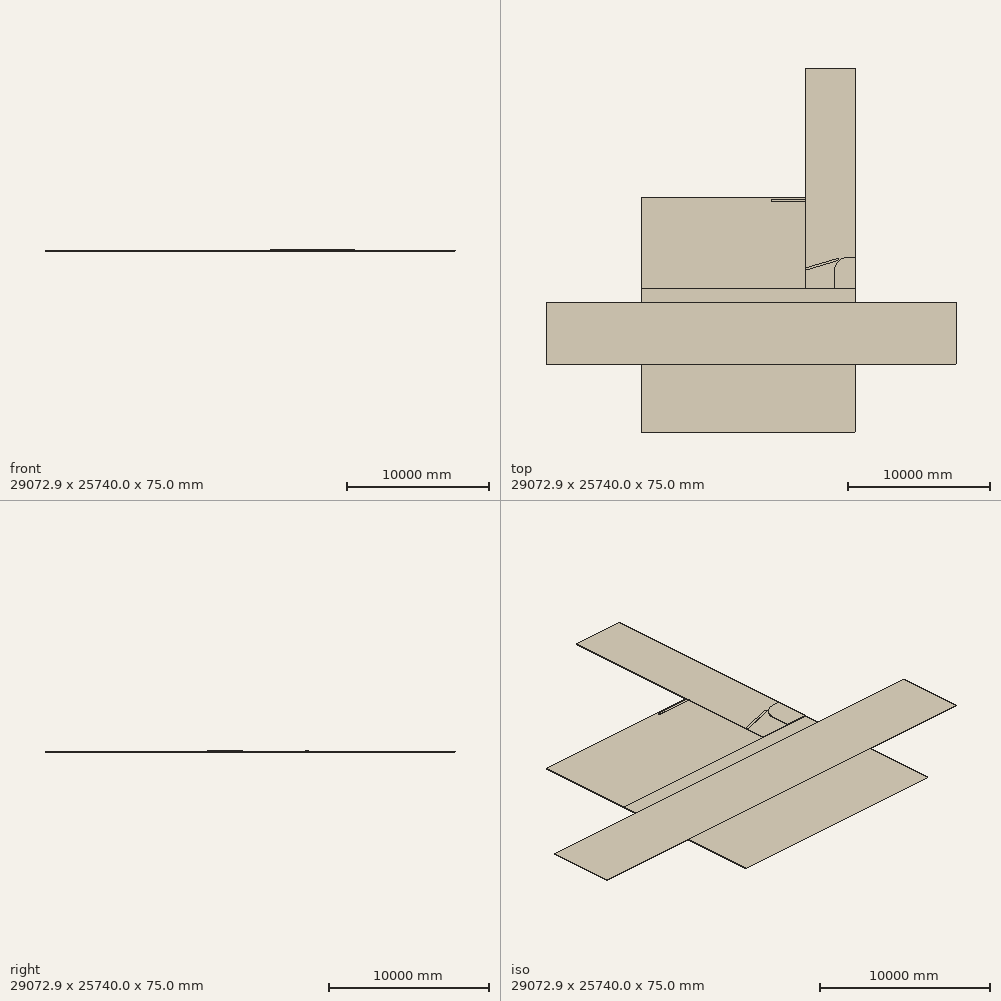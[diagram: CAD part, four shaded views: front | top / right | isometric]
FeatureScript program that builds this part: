
annotation { "Feature Type Name" : "Feature", "Feature Type Description" : "" }
export const myFeature = defineFeature(function(context is Context, id is Id, definition is map)
    precondition{}
    {
        {
            var Q0;
            Q0=qCreatedBy(makeId("Top.planeOp"),FACE);
            var sketch = newSketch(context, id + "F0", { "sketchPlane" : qUnion([Q0])});
            skLineSegment(sketch, "E0", {"start": v(0, 8204.37) * mm, "end": v(0, -7335.63) * mm, "construction": true});
            skLineSegment(sketch, "E1", {"start": v(-1775, 8204.37) * mm, "end": v(1775, 8204.37) * mm});
            skPoint(sketch, "E2", {"position": v(0, 8204.37) * mm});
            skLineSegment(sketch, "E3", {"start": v(-1775, 8204.37) * mm, "end": v(-1775, 7954.37) * mm});
            skLineSegment(sketch, "E4", {"start": v(-1775, 5584.37) * mm, "end": v(-1775, -895.63) * mm});
            skLineSegment(sketch, "E5", {"start": v(-1775, -895.63) * mm, "end": v(-1775, -7335.63) * mm});
            skLineSegment(sketch, "E6", {"start": v(-1775, -7335.63) * mm, "end": v(1775, -7335.63) * mm});
            skLineSegment(sketch, "E7", {"start": v(1775, -7335.63) * mm, "end": v(1775, 8204.37) * mm});
            skLineSegment(sketch, "E8", {"start": v(-1775, 7954.37) * mm, "end": v(-1775, 5584.37) * mm});
            skPoint(sketch, "E9", {"position": v(0, 0) * mm});
            skPoint(sketch, "E10", {"position": v(-1775, -1195.63) * mm});
            skPoint(sketch, "E11", {"position": v(-1775, -3634.03) * mm});
            skPoint(sketch, "E12", {"position": v(-1775, -6072.43) * mm});
            skSolve(sketch);
        }
        {
            var Q0;
            Q0=makeQuery(id+"F0.imprint","IMPRINT",FACE,{"disambiguationData":[TD([[makeQuery(id+"F0.imprint","IMPRINT",EDGE,{"derivedFrom":sQuery(id+"F0.wireOp",EDGE,"E1")}),-1.0]])]});
            extrude(context, id + "F1", {"entities" : qUnion([Q0]), "depth" : 50 * mm, "offsetDistance" : 25 * mm});
        }
        {
            var Q0;
            Q0=makeQuery(id+"F1.opExtrude","CAP_FACE",FACE,{"disambiguationData":[OSD([sQuery(id+"F0.wireOp",EDGE,"E1"),sQuery(id+"F0.wireOp",EDGE,"E3"),sQuery(id+"F0.wireOp",EDGE,"E4"),sQuery(id+"F0.wireOp",EDGE,"E5"),sQuery(id+"F0.wireOp",EDGE,"E6"),sQuery(id+"F0.wireOp",EDGE,"E7"),sQuery(id+"F0.wireOp",EDGE,"E8")])],"isStart":false});
            var sketch = newSketch(context, id + "F2", { "sketchPlane" : qUnion([Q0])});
            skLineSegment(sketch, "E13", {"start": v(275, -7335.63) * mm, "end": v(275, -6145.63) * mm});
            skLineSegment(sketch, "E14", {"start": v(1775, -5145.63) * mm, "end": v(1275, -5145.63) * mm});
            skPoint(sketch, "E15.visualSharp", {"position": v(275, -5145.63) * mm});
            skArc(sketch, "E15.filletArc", {"start": v(1275, -5145.63) * mm, "mid": v(567.9, -5438.53) * mm, "end": v(275, -6145.63) * mm});
            skSolve(sketch);
        }
        {
            var Q0;
            {var subQ3=sQuery(id+"F2.wireOp",EDGE,"E13");Q0=makeQuery(id+"F2.imprint","IMPRINT",FACE,{"disambiguationData":[TD([[makeQuery(id+"F2.imprint","IMPRINT",EDGE,{"derivedFrom":subQ3}),-1.0]])]});}
            extrude(context, id + "F3", {"entities" : qUnion([Q0]), "depth" : 25 * mm, "offsetDistance" : 25 * mm});
        }
        {
            var Q0;
            Q0=makeQuery(id+"F1.opExtrude","CAP_FACE",FACE,{"disambiguationData":[OSD([sQuery(id+"F0.wireOp",EDGE,"E1"),sQuery(id+"F0.wireOp",EDGE,"E3"),sQuery(id+"F0.wireOp",EDGE,"E4"),sQuery(id+"F0.wireOp",EDGE,"E5"),sQuery(id+"F0.wireOp",EDGE,"E6"),sQuery(id+"F0.wireOp",EDGE,"E7"),sQuery(id+"F0.wireOp",EDGE,"E8")])],"isStart":false});
            var sketch = newSketch(context, id + "F4", { "sketchPlane" : qUnion([Q0])});
            skLineSegment(sketch, "E16", {"start": v(-1775, -6072.43) * mm, "end": v(561.65, -5375.4) * mm});
            skLineSegment(sketch, "E17", {"start": v(-1775, -6072.43) * mm, "end": v(-1818.57, -5926.4) * mm});
            skLineSegment(sketch, "E18", {"start": v(-1818.57, -5926.4) * mm, "end": v(518.08, -5229.35) * mm});
            skLineSegment(sketch, "E19", {"start": v(518.08, -5229.35) * mm, "end": v(561.65, -5375.4) * mm});
            skLineSegment(sketch, "E20", {"start": v(-1775, -1195.63) * mm, "end": v(-4213.4, -1190.53) * mm});
            skLineSegment(sketch, "E21", {"start": v(-4213.4, -1190.53) * mm, "end": v(-4213.08, -1038.13) * mm});
            skLineSegment(sketch, "E22", {"start": v(-4213.08, -1038.13) * mm, "end": v(-1774.68, -1043.24) * mm});
            skLineSegment(sketch, "E23", {"start": v(-1774.68, -1043.24) * mm, "end": v(-1775, -1195.63) * mm});
            skSolve(sketch);
        }
        {
            var Q0;
            {var subQ0=sQuery(id+"F4.wireOp",EDGE,"E20");Q0=makeQuery(id+"F4.imprint","IMPRINT",FACE,{"disambiguationData":[TD([[makeQuery(id+"F4.imprint","IMPRINT",EDGE,{"derivedFrom":subQ0}),-1.0]])]});}
            var Q1;
            {var subQ0=sQuery(id+"F4.wireOp",EDGE,"E16");Q1=makeQuery(id+"F4.imprint","IMPRINT",FACE,{"disambiguationData":[TD([[makeQuery(id+"F4.imprint","IMPRINT",EDGE,{"derivedFrom":subQ0}),1.0]])]});}
            extrude(context, id + "F5", {"entities" : qUnion([Q0, Q1]), "depth" : 25 * mm, "offsetDistance" : 25 * mm});
        }
        {
            var Q0;
            Q0=qCreatedBy(makeId("Top.planeOp"),FACE);
            var sketch = newSketch(context, id + "F6", { "sketchPlane" : qUnion([Q0])});
            skLineSegment(sketch, "E24.bottom", {"start": v(-1775, -895.63) * mm, "end": v(-13375, -895.63) * mm});
            skLineSegment(sketch, "E24.top", {"start": v(-1775, -7335.63) * mm, "end": v(-13375, -7335.63) * mm});
            skLineSegment(sketch, "E24.left", {"start": v(-1775, -895.63) * mm, "end": v(-1775, -7335.63) * mm});
            skLineSegment(sketch, "E24.right", {"start": v(-13375, -895.63) * mm, "end": v(-13375, -7335.63) * mm});
            skSolve(sketch);
        }
        {
            var Q0;
            Q0=makeQuery(id+"F6.imprint","IMPRINT",FACE,{"disambiguationData":[TD([[makeQuery(id+"F6.imprint","IMPRINT",EDGE,{"derivedFrom":sQuery(id+"F6.wireOp",EDGE,"E24.bottom")}),1.0]])]});
            extrude(context, id + "F7", {"entities" : qUnion([Q0]), "depth" : 25 * mm, "offsetDistance" : 25 * mm});
        }
        {
            var Q0;
            Q0=qCreatedBy(makeId("Top.planeOp"),FACE);
            var sketch = newSketch(context, id + "F8", { "sketchPlane" : qUnion([Q0])});
            skLineSegment(sketch, "E25.bottom", {"start": v(-13375, -7335.63) * mm, "end": v(1775, -7335.63) * mm});
            skLineSegment(sketch, "E25.top", {"start": v(-13375, -8335.63) * mm, "end": v(1775, -8335.63) * mm});
            skLineSegment(sketch, "E25.left", {"start": v(-13375, -7335.63) * mm, "end": v(-13375, -8335.63) * mm});
            skLineSegment(sketch, "E25.right", {"start": v(1775, -7335.63) * mm, "end": v(1775, -8335.63) * mm});
            skSolve(sketch);
        }
        {
            var Q0;
            Q0=makeQuery(id+"F8.imprint","IMPRINT",FACE,{"disambiguationData":[TD([[makeQuery(id+"F8.imprint","IMPRINT",EDGE,{"derivedFrom":sQuery(id+"F8.wireOp",EDGE,"E25.bottom")}),-1.0]])]});
            extrude(context, id + "F9", {"entities" : qUnion([Q0]), "depth" : 25 * mm, "offsetDistance" : 25 * mm});
        }
        {
            var Q0;
            Q0=qCreatedBy(makeId("Top.planeOp"),FACE);
            var sketch = newSketch(context, id + "F10", { "sketchPlane" : qUnion([Q0])});
            skLineSegment(sketch, "E26.bottom", {"start": v(-20145.32, -8335.63) * mm, "end": v(8927.57, -8335.63) * mm});
            skLineSegment(sketch, "E26.top", {"start": v(-20145.32, -12735.63) * mm, "end": v(8927.57, -12735.63) * mm});
            skLineSegment(sketch, "E26.left", {"start": v(-20145.32, -8335.63) * mm, "end": v(-20145.32, -12735.63) * mm});
            skLineSegment(sketch, "E26.right", {"start": v(8927.57, -8335.63) * mm, "end": v(8927.57, -12735.63) * mm});
            skSolve(sketch);
        }
        {
            var Q0;
            Q0=makeQuery(id+"F10.imprint","IMPRINT",FACE,{"disambiguationData":[TD([[makeQuery(id+"F10.imprint","IMPRINT",EDGE,{"derivedFrom":sQuery(id+"F10.wireOp",EDGE,"E26.bottom")}),-1.0]])]});
            extrude(context, id + "F11", {"entities" : qUnion([Q0]), "depth" : 25 * mm, "offsetDistance" : 25 * mm});
        }
        {
            var Q0;
            Q0=qCreatedBy(makeId("Top.planeOp"),FACE);
            var sketch = newSketch(context, id + "F12", { "sketchPlane" : qUnion([Q0])});
            skLineSegment(sketch, "E27.bottom", {"start": v(-13375, -12735.63) * mm, "end": v(1775, -12735.63) * mm});
            skLineSegment(sketch, "E27.top", {"start": v(-13375, -17535.63) * mm, "end": v(1775, -17535.63) * mm});
            skLineSegment(sketch, "E27.left", {"start": v(-13375, -12735.63) * mm, "end": v(-13375, -17535.63) * mm});
            skLineSegment(sketch, "E27.right", {"start": v(1775, -12735.63) * mm, "end": v(1775, -17535.63) * mm});
            skSolve(sketch);
        }
        {
            var Q0;
            Q0=makeQuery(id+"F12.imprint","IMPRINT",FACE,{"disambiguationData":[TD([[makeQuery(id+"F12.imprint","IMPRINT",EDGE,{"derivedFrom":sQuery(id+"F12.wireOp",EDGE,"E27.bottom")}),-1.0]])]});
            extrude(context, id + "F13", {"entities" : qUnion([Q0]), "depth" : 25 * mm, "offsetDistance" : 25 * mm});
        }
    });
